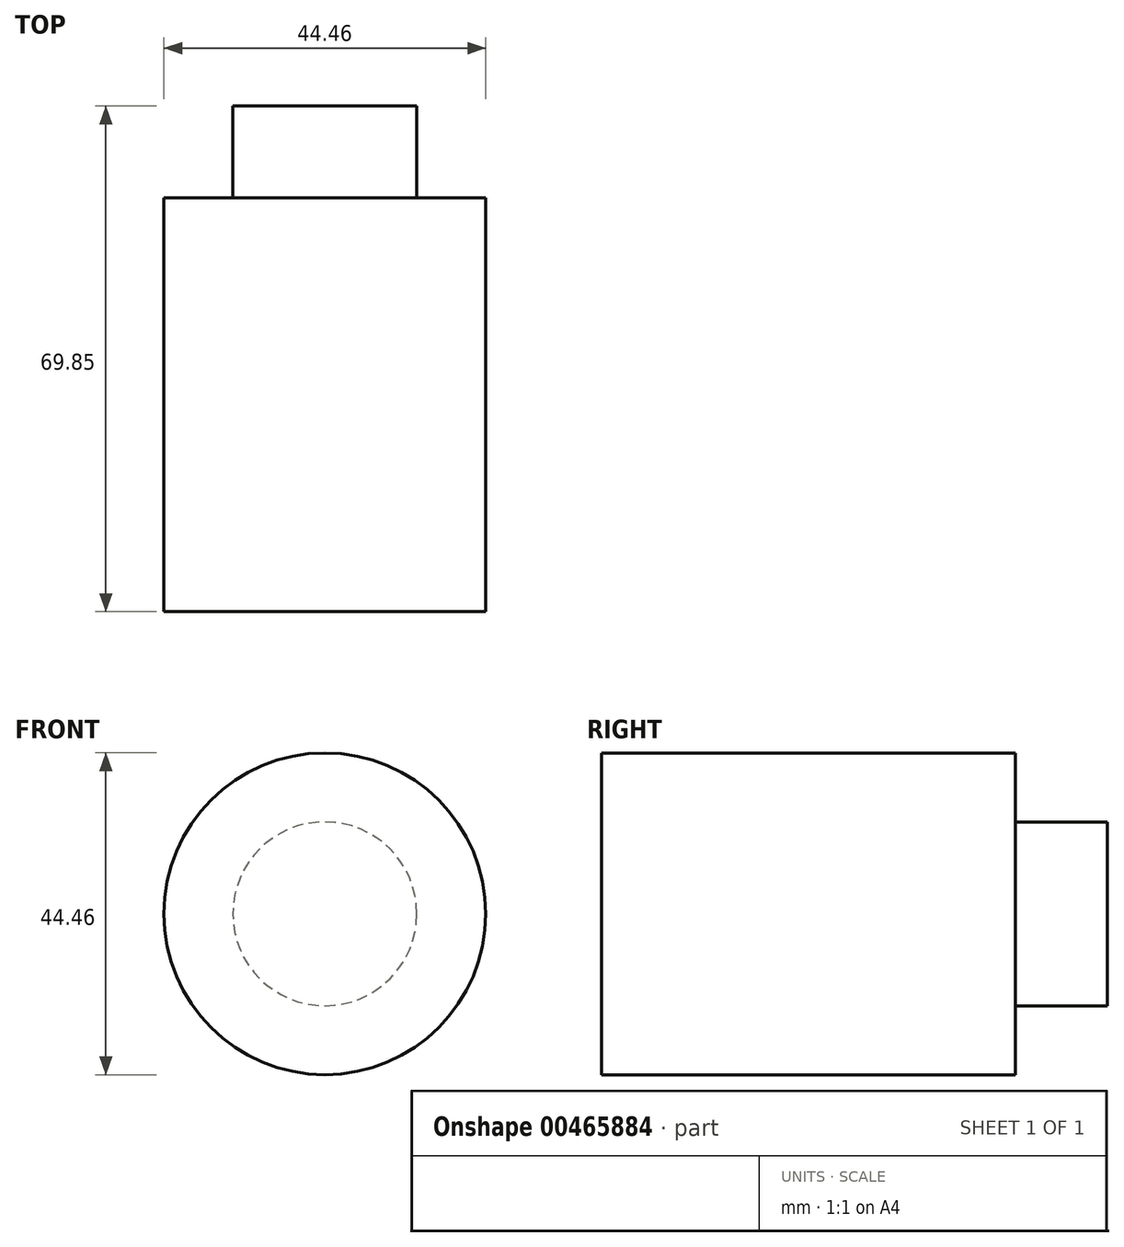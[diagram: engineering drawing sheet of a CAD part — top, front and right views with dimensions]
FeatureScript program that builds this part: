
annotation { "Feature Type Name" : "Feature", "Feature Type Description" : "" }
export const myFeature = defineFeature(function(context is Context, id is Id, definition is map)
    precondition{}
    {
        {
            var Q0;
            Q0=qCreatedBy(makeId("Front.planeOp"),FACE);
            var sketch = newSketch(context, id + "F0", { "sketchPlane" : qUnion([Q0])});
            skCircle(sketch, "E0", {"center": v(0, 0) * mm, "radius": 22.23 * mm});
            skSolve(sketch);
        }
        {
            var Q0;
            Q0=makeQuery(id+"F0.imprint","IMPRINT",FACE,{"disambiguationData":[TD([[makeQuery(id+"F0.imprint","IMPRINT",EDGE,{"derivedFrom":sQuery(id+"F0.wireOp",EDGE,"E0")}),1.0]])]});
            extrude(context, id + "F1", {"entities" : qUnion([Q0]), "depth" : 57.15 * mm, "offsetDistance" : 25.4 * mm});
        }
        {
            var Q0;
            Q0=qCreatedBy(makeId("Front.planeOp"),FACE);
            var sketch = newSketch(context, id + "F2", { "sketchPlane" : qUnion([Q0])});
            skCircle(sketch, "E1", {"center": v(0, 0) * mm, "radius": 12.7 * mm});
            skSolve(sketch);
        }
        {
            var Q0;
            Q0=makeQuery(id+"F2.imprint","IMPRINT",FACE,{"disambiguationData":[TD([[makeQuery(id+"F2.imprint","IMPRINT",EDGE,{"derivedFrom":sQuery(id+"F2.wireOp",EDGE,"E1")}),1.0]])]});
            extrude(context, id + "F3", {"entities" : qUnion([Q0]), "operationType" : NewBodyOperationType.ADD, "depth" : -12.7 * mm, "offsetDistance" : 25.4 * mm});
        }
    });
